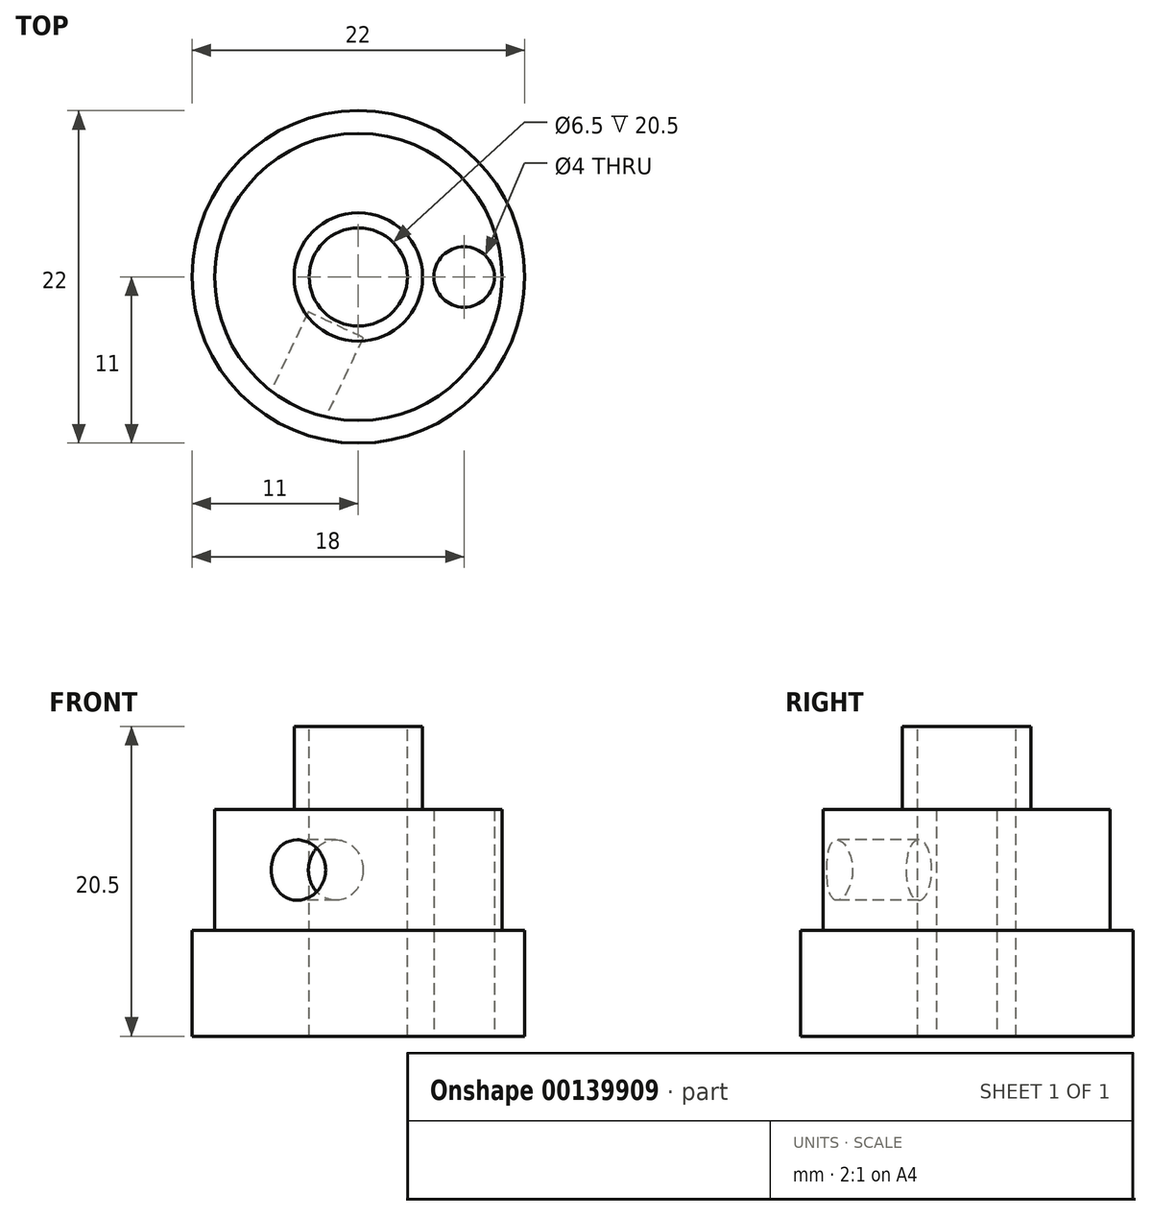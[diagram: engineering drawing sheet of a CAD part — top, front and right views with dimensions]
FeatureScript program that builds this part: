
annotation { "Feature Type Name" : "Feature", "Feature Type Description" : "" }
export const myFeature = defineFeature(function(context is Context, id is Id, definition is map)
    precondition{}
    {
        {
            var Q0;
            Q0=qCreatedBy(makeId("Top.planeOp"),FACE);
            var sketch = newSketch(context, id + "F0", { "sketchPlane" : qUnion([Q0])});
            skCircle(sketch, "E0", {"center": v(0, 0) * mm, "radius": 11 * mm});
            skSolve(sketch);
        }
        {
            var Q0;
            Q0 = qSketchRegion(id + "F0", true);
            extrude(context, id + "F1", {"entities" : qUnion([Q0]), "depth" : 7 * mm});
        }
        {
            var Q0;
            Q0=makeQuery(id+"F1.opExtrude","CAP_FACE",FACE,{"disambiguationData":[OSD([sQuery(id+"F0.wireOp",EDGE,"E0")])],"isStart":false});
            var sketch = newSketch(context, id + "F2", { "sketchPlane" : qUnion([Q0])});
            skCircle(sketch, "E1", {"center": v(0, 0) * mm, "radius": 9.5 * mm});
            skSolve(sketch);
        }
        {
            var Q0;
            Q0 = qSketchRegion(id + "F2", true);
            var Q1;
            Q1 = qSketchRegion(id + "F4", true);
            extrude(context, id + "F3", {"entities" : qUnion([Q0, Q1]), "operationType" : NewBodyOperationType.ADD, "depth" : 8 * mm});
        }
        {
            var Q0;
            Q0=makeQuery(id+"F3.opExtrude","CAP_FACE",FACE,{"disambiguationData":[OSD([sQuery(id+"F2.wireOp",EDGE,"E1")])],"isStart":false});
            var sketch = newSketch(context, id + "F4", { "sketchPlane" : qUnion([Q0])});
            skCircle(sketch, "E2", {"center": v(0, 0) * mm, "radius": 4.25 * mm});
            skSolve(sketch);
        }
        {
            var Q0;
            Q0 = qSketchRegion(id + "F4", true);
            extrude(context, id + "F5", {"entities" : qUnion([Q0]), "operationType" : NewBodyOperationType.ADD, "depth" : 5.5 * mm});
        }
        {
            var Q0;
            Q0=makeQuery(id+"F5.opExtrude","CAP_FACE",FACE,{"disambiguationData":[OSD([sQuery(id+"F4.wireOp",EDGE,"E2")])],"isStart":false});
            var sketch = newSketch(context, id + "F6", { "sketchPlane" : qUnion([Q0])});
            skCircle(sketch, "E3", {"center": v(0, 0) * mm, "radius": 3.25 * mm});
            skSolve(sketch);
        }
        {
            var Q0;
            Q0=makeQuery(id+"F6.imprint","IMPRINT",FACE,{"disambiguationData":[TD([[makeQuery(id+"F6.imprint","IMPRINT",EDGE,{"derivedFrom":sQuery(id+"F6.wireOp",EDGE,"E3")}),1.0]])]});
            extrude(context, id + "F7", {"entities" : qUnion([Q0]), "operationType" : NewBodyOperationType.REMOVE, "endBound" : BoundingType.THROUGH_ALL, "oppositeDirection" : true, "depth" : 25 * mm});
        }
        {
            var Q0;
            Q0=makeQuery(id+"F1.opExtrude","CAP_FACE",FACE,{"disambiguationData":[OSD([sQuery(id+"F0.wireOp",EDGE,"E0")])],"isStart":true});
            var sketch = newSketch(context, id + "F8", { "sketchPlane" : qUnion([Q0])});
            skCircle(sketch, "E4", {"center": v(7, 0) * mm, "radius": 2 * mm});
            skSolve(sketch);
        }
        {
            var Q0;
            Q0 = qSketchRegion(id + "F8", true);
            extrude(context, id + "F9", {"entities" : qUnion([Q0]), "operationType" : NewBodyOperationType.REMOVE, "endBound" : BoundingType.THROUGH_ALL, "oppositeDirection" : true, "depth" : 25 * mm});
        }
        {
            var Q0;
            Q0=makeQuery(id+"F3.opExtrude","CAP_FACE",FACE,{"disambiguationData":[OSD([sQuery(id+"F2.wireOp",EDGE,"E1")])],"isStart":false});
            var sketch = newSketch(context, id + "F10", { "sketchPlane" : qUnion([Q0])});
            skCircle(sketch, "E5.0", {"center": v(7, 0) * mm, "radius": 2 * mm});
            skLineSegment(sketch, "E6", {"start": v(7, 0) * mm, "end": v(-4.05, -8.6) * mm, "construction": true});
            skLineSegment(sketch, "E7", {"start": v(-6.2, -7.57) * mm, "end": v(-1.9, -9.6) * mm, "construction": true});
            skSolve(sketch);
        }
        {
            var Q0;
            Q0=sQuery(id+"F10.wireOp",EDGE,"E7");
            cPlane(context, id + "F11", {"entities" : qUnion([Q0]), "cplaneType" : CPlaneType.LINE_ANGLE, "offset" : 25 * mm, "angle" : 0 * degree, "width" : 150 * mm, "height" : 150 * mm});
        }
        {
            var Q0;
            Q0=qCreatedBy(id+"F11.planeOp",FACE);
            var sketch = newSketch(context, id + "F12", { "sketchPlane" : qUnion([Q0])});
            skPoint(sketch, "E8.0", {"position": v(0, 15) * mm});
            skCircle(sketch, "E9", {"center": v(0, 11) * mm, "radius": 2 * mm});
            skSolve(sketch);
        }
        {
            var Q0;
            Q0 = qSketchRegion(id + "F12", true);
            extrude(context, id + "F13", {"entities" : qUnion([Q0]), "operationType" : NewBodyOperationType.REMOVE, "depth" : 6 * mm});
        }
    });
